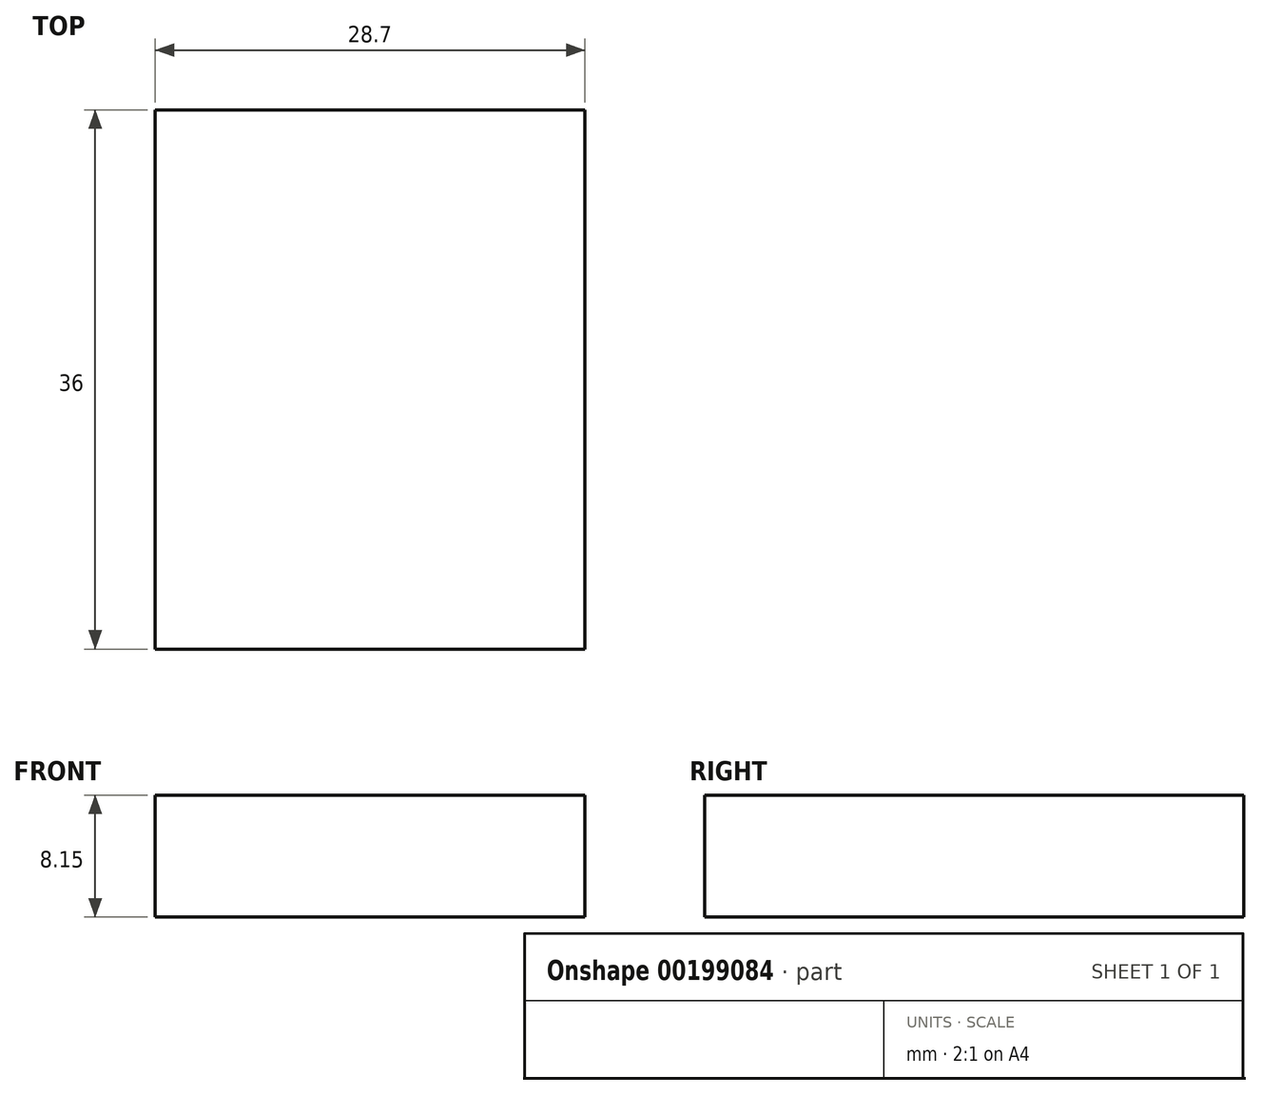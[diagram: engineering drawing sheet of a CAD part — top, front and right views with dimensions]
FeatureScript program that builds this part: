
annotation { "Feature Type Name" : "Feature", "Feature Type Description" : "" }
export const myFeature = defineFeature(function(context is Context, id is Id, definition is map)
    precondition{}
    {
        {
            var Q0;
            Q0=qCreatedBy(makeId("Top.planeOp"),FACE);
            var sketch = newSketch(context, id + "F0", { "sketchPlane" : qUnion([Q0])});
            skLineSegment(sketch, "E0.bottom", {"start": v(14.35, 18) * mm, "end": v(-14.35, 18) * mm});
            skLineSegment(sketch, "E0.top", {"start": v(14.35, -18) * mm, "end": v(-14.35, -18) * mm});
            skLineSegment(sketch, "E0.left", {"start": v(14.35, 18) * mm, "end": v(14.35, -18) * mm});
            skLineSegment(sketch, "E0.right", {"start": v(-14.35, 18) * mm, "end": v(-14.35, -18) * mm});
            skPoint(sketch, "E0.middle", {"position": v(0, 0) * mm});
            skSolve(sketch);
        }
        {
            var Q0;
            Q0 = qSketchRegion(id + "F0", true);
            extrude(context, id + "F1", {"entities" : qUnion([Q0]), "depth" : 8.15 * mm});
        }
    });
